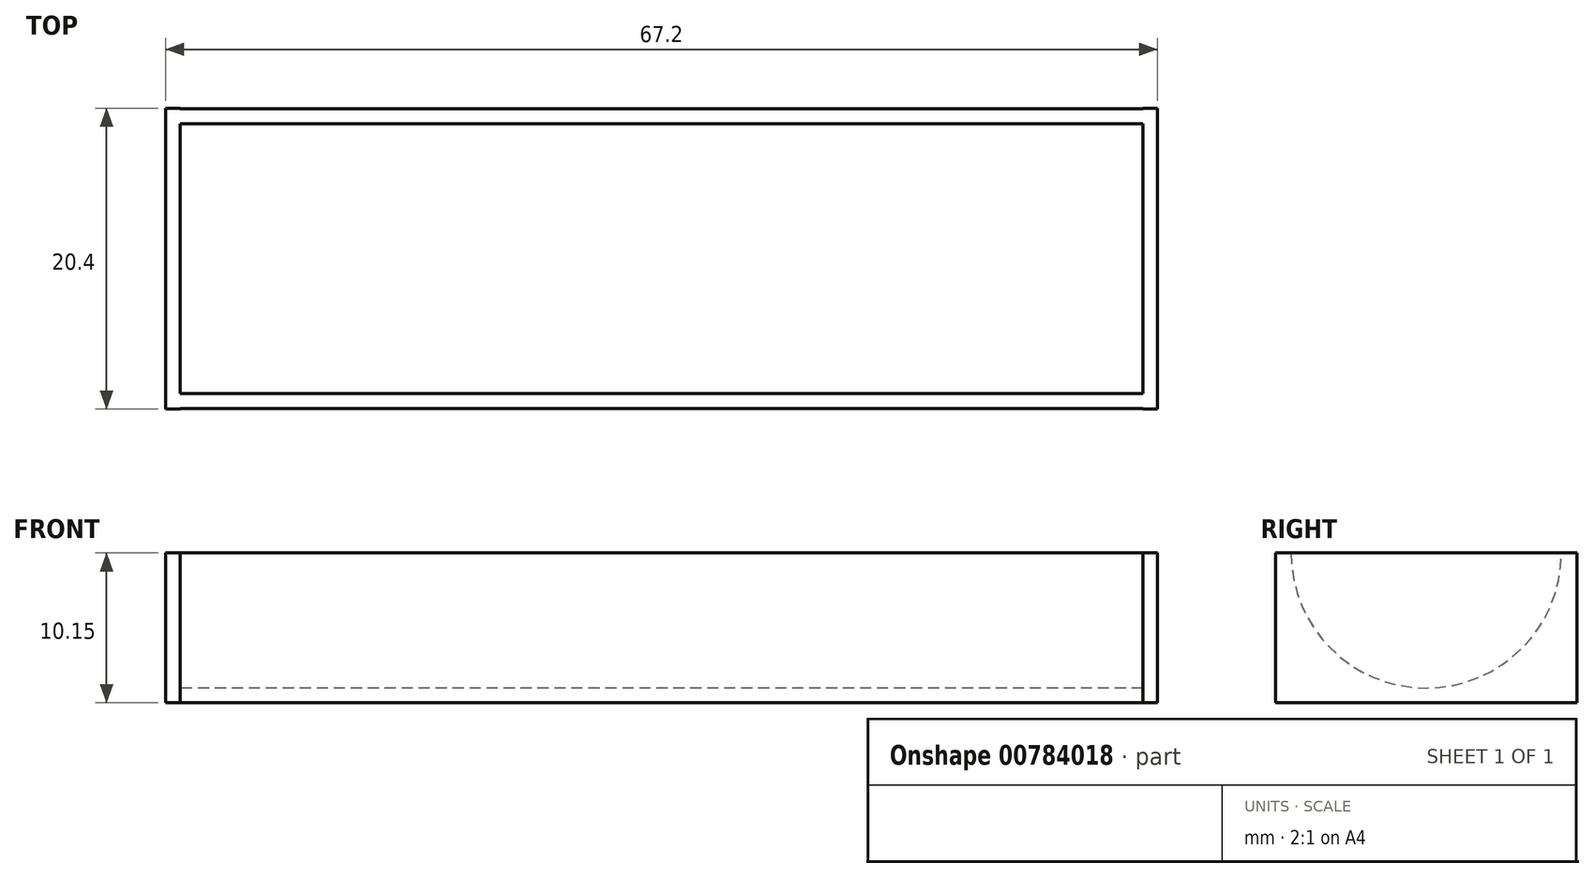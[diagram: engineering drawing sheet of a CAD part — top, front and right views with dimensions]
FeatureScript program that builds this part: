
annotation { "Feature Type Name" : "Feature", "Feature Type Description" : "" }
export const myFeature = defineFeature(function(context is Context, id is Id, definition is map)
    precondition{}
    {
        {
            var Q0;
            Q0=qCreatedBy(makeId("Top.planeOp"),FACE);
            var sketch = newSketch(context, id + "F0", { "sketchPlane" : qUnion([Q0])});
            skLineSegment(sketch, "E0.bottom", {"start": v(32.6, -9.2) * mm, "end": v(-32.6, -9.2) * mm, "construction": true});
            skLineSegment(sketch, "E0.top", {"start": v(32.6, 9.2) * mm, "end": v(-32.6, 9.2) * mm, "construction": true});
            skLineSegment(sketch, "E0.left", {"start": v(32.6, -9.2) * mm, "end": v(32.6, 9.2) * mm});
            skLineSegment(sketch, "E0.right", {"start": v(-32.6, -9.2) * mm, "end": v(-32.6, 9.2) * mm});
            skPoint(sketch, "E0.middle", {"position": v(0, 0) * mm});
            skLineSegment(sketch, "E1.bottom", {"start": v(33.6, -10.2) * mm, "end": v(32.6, -10.2) * mm});
            skLineSegment(sketch, "E1.top", {"start": v(33.6, 10.2) * mm, "end": v(32.6, 10.2) * mm});
            skLineSegment(sketch, "E1.left", {"start": v(33.6, -10.2) * mm, "end": v(33.6, 10.2) * mm});
            skLineSegment(sketch, "E1.right", {"start": v(-33.6, -10.2) * mm, "end": v(-33.6, 10.2) * mm});
            skLineSegment(sketch, "E2", {"start": v(-32.6, 9.2) * mm, "end": v(-32.6, 10.2) * mm});
            skLineSegment(sketch, "E3", {"start": v(-32.6, -9.2) * mm, "end": v(-32.6, -10.2) * mm});
            skLineSegment(sketch, "E4", {"start": v(32.6, -9.2) * mm, "end": v(32.6, -10.2) * mm});
            skLineSegment(sketch, "E5", {"start": v(32.6, 9.2) * mm, "end": v(32.6, 10.2) * mm});
            skLineSegment(sketch, "E6.trimOffspring", {"start": v(-32.6, -10.2) * mm, "end": v(-33.6, -10.2) * mm});
            skLineSegment(sketch, "E7.trimOffspring", {"start": v(-32.6, 10.2) * mm, "end": v(-33.6, 10.2) * mm});
            skSolve(sketch);
        }
        {
            var Q0;
            Q0=qCreatedBy(makeId("Right.planeOp"),FACE);
            var sketch = newSketch(context, id + "F1", { "sketchPlane" : qUnion([Q0])});
            skArc(sketch, "E8", {"start": v(-9.15, 10.15) * mm, "mid": v(0, 1) * mm, "end": v(9.15, 10.15) * mm});
            skLineSegment(sketch, "E9", {"start": v(9.15, 10.15) * mm, "end": v(-9.15, 10.15) * mm, "construction": true});
            skLineSegment(sketch, "E10", {"start": v(9.15, 10.15) * mm, "end": v(10.15, 10.15) * mm});
            skLineSegment(sketch, "E11", {"start": v(10.15, 10.15) * mm, "end": v(10.15, 0) * mm});
            skLineSegment(sketch, "E12", {"start": v(10.15, 0) * mm, "end": v(-10.15, 0) * mm});
            skLineSegment(sketch, "E13", {"start": v(-10.15, 0) * mm, "end": v(-10.15, 10.15) * mm});
            skLineSegment(sketch, "E14", {"start": v(-10.15, 10.15) * mm, "end": v(-9.15, 10.15) * mm});
            skSolve(sketch);
        }
        {
            var Q0;
            {var subQ4=sQuery(id+"F1.wireOp",EDGE,"E13");Q0=makeQuery(id+"F1.imprint","IMPRINT",FACE,{"disambiguationData":[TD([[makeQuery(id+"F1.imprint","IMPRINT",EDGE,{"derivedFrom":subQ4}),-1.0]])]});}
            var Q1;
            Q1=sQuery(id+"F1.wireOp",EDGE,"E9");
            extrude(context, id + "F2", {"entities" : qUnion([Q0]), "surfaceEntities" : qUnion([Q1]), "endBound" : BoundingType.SYMMETRIC, "depth" : 65.2 * mm, "offsetDistance" : 25 * mm});
        }
        {
            var Q0;
            Q0=makeQuery(id+"F0.imprint","IMPRINT",FACE,{"disambiguationData":[TD([[makeQuery(id+"F0.imprint","IMPRINT",EDGE,{"derivedFrom":sQuery(id+"F0.wireOp",EDGE,"E0.right")}),1.0]])]});
            var Q1;
            Q1=makeQuery(id+"F0.imprint","IMPRINT",FACE,{"disambiguationData":[TD([[makeQuery(id+"F0.imprint","IMPRINT",EDGE,{"derivedFrom":sQuery(id+"F0.wireOp",EDGE,"E0.left")}),-1.0]])]});
            var Q2;
            Q2=makeQuery(id+"F2.opExtrude","SWEPT_FACE",FACE,{"disambiguationData":[OSD([sQuery(id+"F1.wireOp",EDGE,"E14")])]});
            extrude(context, id + "F3", {"entities" : qUnion([Q0, Q1]), "operationType" : NewBodyOperationType.ADD, "endBound" : BoundingType.UP_TO_SURFACE, "depth" : 25 * mm, "endBoundEntityFace" : qUnion([Q2]), "offsetDistance" : 25 * mm});
        }
    });
